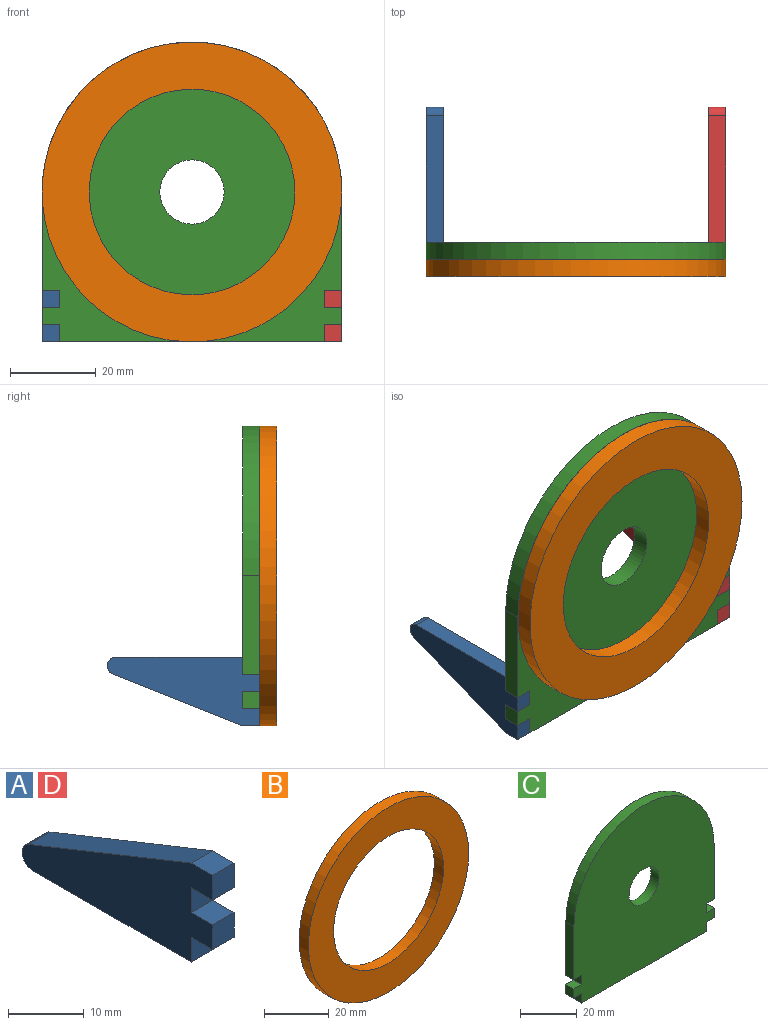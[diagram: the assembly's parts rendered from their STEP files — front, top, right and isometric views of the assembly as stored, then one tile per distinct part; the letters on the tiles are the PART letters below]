
ASSEMBLY  parts=4 mates=3
PART A: 13 faces, bbox 4x35.6x16 mm
  f0: plane 4x4mm, normal (0,0,-1), area 16mm2, adj f1,f10,f11,f12
  f1: plane 4x4mm, normal (0,-1,0), area 16mm2, adj f0,f2,f11,f12
  f2: plane 29.62x4mm, normal (0,0,-1), area 118.5mm2, adj f1,f3,f11,f12
  f3: cylinder r=2mm len=4mm, axis (-1,0,0), area 22.1mm2, adj f2,f4,f11,f12
  f4: plane 30.36x12.14mm, normal (0,0.37,0.93), area 130.8mm2, adj f3,f5,f11,f12
  f5: plane 4x4mm, normal (0,0,1), area 16mm2, adj f4,f6,f11,f12
  f6: plane 4x4mm, normal (0,-1,0), area 16mm2, adj f5,f7,f11,f12
  f7: plane 4x4mm, normal (0,0,-1), area 16mm2, adj f6,f8,f11,f12
  f8: plane 4x4mm, normal (0,-1,0), area 16mm2, adj f7,f9,f11,f12
  f9: plane 4x4mm, normal (0,0,1), area 16mm2, adj f8,f10,f11,f12
  f10: plane 4x4mm, normal (0,-1,0), area 16mm2, adj f0,f9,f11,f12
  f11: plane 35.62x16mm, normal (1,0,0), area 336.8mm2, adj f0,f1,f2,f3,f4,f5,f6,f7
  f12: plane 35.62x16mm, normal (-1,0,0), area 336.8mm2, adj f0,f1,f2,f3,f4,f5,f6,f7
PART B: 4 faces, bbox 70x4x70 mm
  f0: cylinder r=24mm len=48mm, axis (0,1,0), area 603.2mm2, adj f2,f3
  f1: cylinder r=35mm len=70mm, axis (0,1,0), area 879.6mm2, adj f2,f3
  f2: plane 70x70mm, normal (0,-1,0), area 2038.9mm2, adj f0,f1
  f3: plane 70x70mm, normal (0,1,0), area 2038.9mm2, adj f0,f1
PART C: 19 faces, bbox 70x4x70 mm
  f0: plane 62x4mm, normal (0,0,-1), area 248mm2, adj f1,f16,f17,f18
  f1: plane 4x4mm, normal (1,0,0), area 16mm2, adj f0,f2,f17,f18
  f2: plane 4x4mm, normal (0,0,-1), area 16mm2, adj f1,f3,f17,f18
  f3: plane 4x4mm, normal (1,0,0), area 16mm2, adj f2,f4,f17,f18
  f4: plane 4x4mm, normal (0,0,1), area 16mm2, adj f3,f5,f17,f18
  f5: plane 4x4mm, normal (1,0,0), area 16mm2, adj f4,f6,f17,f18
  f6: plane 4x4mm, normal (0,0,-1), area 16mm2, adj f5,f7,f17,f18
  f7: plane 23x4mm, normal (1,0,0), area 92mm2, adj f6,f8,f17,f18
  f8: cylinder r=35mm len=70mm, axis (0,1,0), area 439.8mm2, adj f7,f9,f17,f18
  f9: plane 23x4mm, normal (-1,0,0), area 92mm2, adj f8,f10,f17,f18
  f10: plane 4x4mm, normal (0,0,-1), area 16mm2, adj f9,f11,f17,f18
  f11: plane 4x4mm, normal (-1,0,0), area 16mm2, adj f10,f12,f17,f18
  f12: plane 4x4mm, normal (0,0,1), area 16mm2, adj f11,f13,f17,f18
  f13: plane 4x4mm, normal (-1,0,0), area 16mm2, adj f12,f14,f17,f18
  f14: plane 4x4mm, normal (0,0,-1), area 16mm2, adj f13,f16,f17,f18
  f15: cylinder r=7.5mm len=15mm, axis (0,1,0), area 188.5mm2, adj f17,f18
  f16: plane 4x4mm, normal (-1,0,0), area 16mm2, adj f0,f14,f17,f18
  f17: plane 70x70mm, normal (0,-1,0), area 4133.5mm2, adj f0,f1,f2,f3,f4,f5,f6,f7
  f18: plane 70x70mm, normal (0,1,0), area 4133.5mm2, adj f0,f1,f2,f3,f4,f5,f6,f7
PART D: same geometry as A
PLACE A rot(axis=(0,1,0),180deg) t=(-60.84,-7.49,-7.4)mm
PLACE B t=(-29.84,-7.49,11.6)mm
PLACE C t=(-29.84,-3.49,11.6)mm
PLACE D rot(axis=(0,1,0),180deg) t=(5.16,-7.49,-7.4)mm
MATE fastened C.f8 <-> B.f0  axis (0,-1,0) through (-29.84,-7.49,11.6)mm
MATE fastened D.f0 <-> C.f6  axis (0,0,1) through (3.16,-5.49,-11.4)mm
MATE fastened A.f0 <-> C.f10  axis (0,0,1) through (-62.84,-5.49,-11.4)mm
